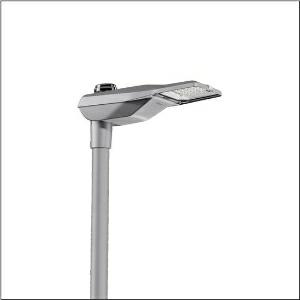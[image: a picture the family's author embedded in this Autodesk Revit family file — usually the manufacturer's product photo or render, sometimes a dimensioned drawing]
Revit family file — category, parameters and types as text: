
# Revit family: streetlight_sl_21_micro___p0_8a_5xe5u57n08db_dcc6
name_source: partatom
category: Lighting Fixtures
units: mm (PartAtom-declared; Revit-internal decimal feet)

## family parameters
Cut with Voids When Loaded = No
Host = Face
Light Source = No
Part Type = Normal
Room Calculation Point = No
Round Connector Dimension = Use Diameter
Shared = No

## types (1)
- --- (1 x LED, 4340 lm, 39.1 W, 3000K)
    Apparent Load = 39 VA
    CIE Flux Codes = 33 69 96 100 100
    Color Rendering = 80
    Color Temperature = 3000K
    Default Elevation = 1800 mm
    Description = Streetlight SL 21 micro, mast luminaire, primary light control with lens, of PMMA, primary optical cover: cover, of toughened safety glass, transparent, light distribution: P0.8a, light emission: direct distribution, primary light characteristic: asymmetric, installation type: post-top, LED, 3G 1.5mm², High Power LED, rated luminous flux: 4.340lm, luminous efficacy: 111lm/W, light colour: 830, colour temperature: 3000K, control gear: NEMA (7pin), control: flexible luminous flux parameterisation, time-dependent luminous flux control, constant luminous flux control, pre-setting: linear dimming characteristic, overheat protection, mains connection: 230..240V, AC, 50/60Hz, connection cable pre-assembled, cable length: 6,5m, wiring characteristics: H07RN-F, start of lifetime: 39W, end of service life: 41W, reduction: 18W, luminaire housing, of diecast aluminium (EN AC-44300), powder-coated, SITECO metallic grey (DB 702S), corrosivity category C5 high according to DIN EN ISO 12944, multi-level sealing system, sealing non-destructively replaceable, inclination adjustable: 0°, 5°, 10°, 15°, length: 528mm, width: 235mm, height: 110mm, spigot size: 76/60mm (post-top), mounting height: 4..8m, protection rating (complete): IP66, insulation class (complete): insulation class I (protective earthing), certification: CE, ENEC, ENEC+, VDE, impact resistance: IK10, permissible operating ambient temperature for outdoor applications: -40..+50°C, standard-compliant lighting for roads and squares, packaging unit: 1 piece

Light Distribution: P0.8a
    Height = 110 mm
    Lamp = 1 x LED
    Lamp Light Flux = 4340 lm
    Lamp Power = 39.1 W
    Lamp count = 1
    Length = 528 mm
    Luminous efficacy = 111 lm/W
    Manufacturer = Siteco
    ModVariant = No
    Model = 5XE5U57N08DB
    Number of Poles = 1
    OnlyDefault = Yes
    Power Factor = 1
    Product Name = Streetlight SL 21 micro | P0.8a
    Product group = mast luminaire | pylon top
    ProductGroupID = 6100
    Protection Class = Protection class I
    Protection Degree = IP 66
    RLX_Detail_Level = 1
    RLX_Emergency_Light_Flux = 0 lm
    RLX_Emergency_Type = 0
    RLX_Emergency_Type_DB = No
    RlxData = <blob elided: 98361 chars, md5=b29b400b>
    Socket = socket
    Standby Power = 0 W
    System Light Flux = 4340 lm
    System Power = 39 W
    Type Comments = factory setting: luminous flux: 100 % | dim-lin: 254 | 765 mA
    Type Image = l_1294375.jpg
    URL = http://relux.com
    VarID = @adj_081471
    Voltage = 0 V
    Weight = 0.00 kg
    Width = 235 mm

## geometry (parser evidence)
native form markers: Blend x4, Sweep x10
no freeform markers — native parametric forms only
